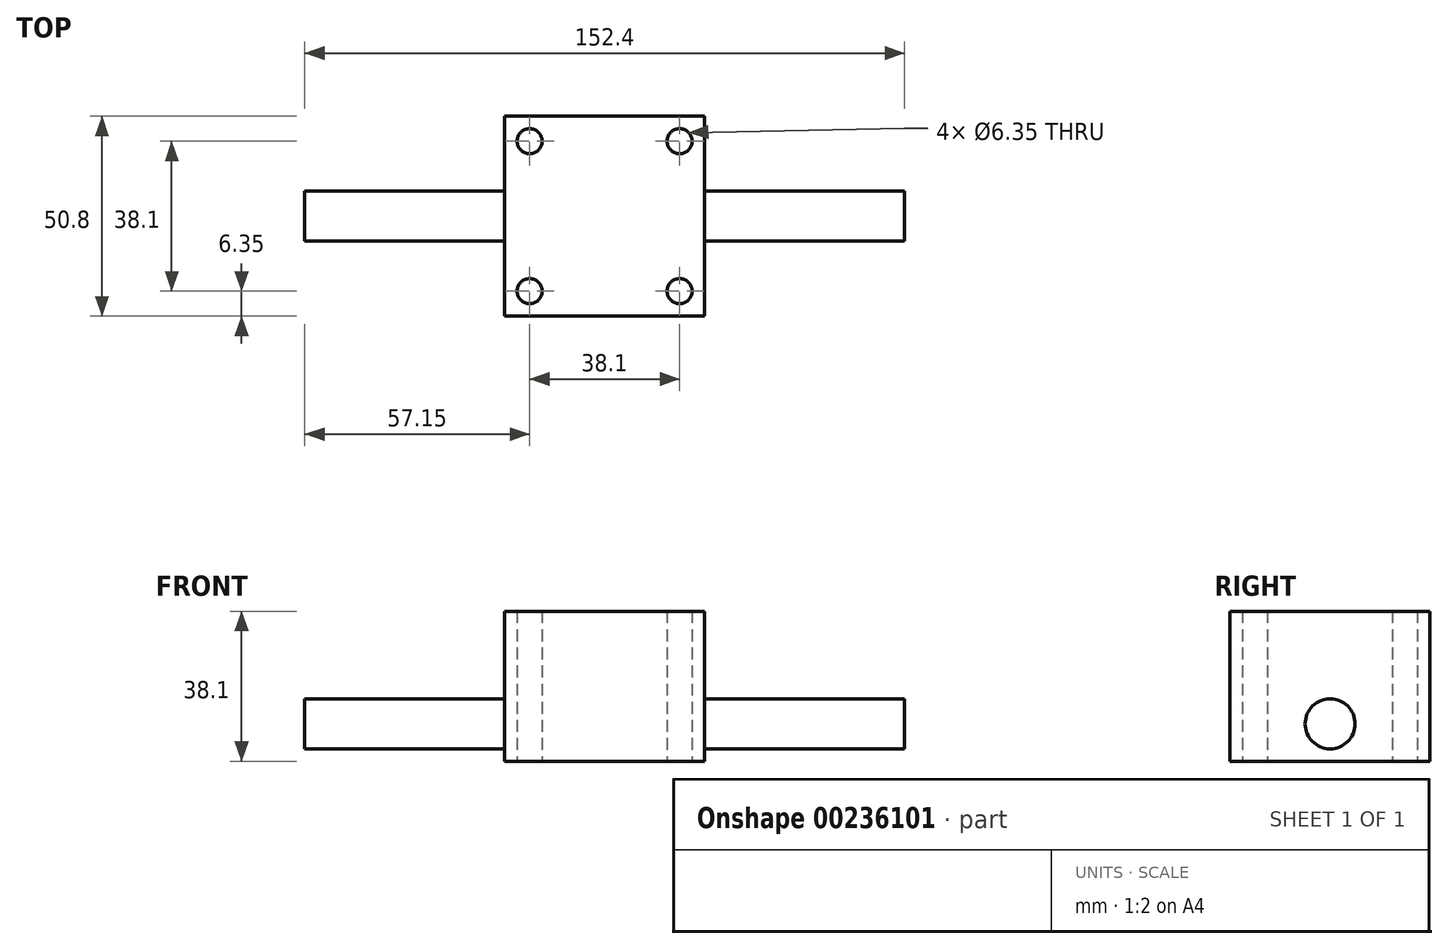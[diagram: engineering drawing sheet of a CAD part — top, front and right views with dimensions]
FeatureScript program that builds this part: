
annotation { "Feature Type Name" : "Feature", "Feature Type Description" : "" }
export const myFeature = defineFeature(function(context is Context, id is Id, definition is map)
    precondition{}
    {
        {
            var Q0;
            Q0=qCreatedBy(makeId("Top.planeOp"),FACE);
            var sketch = newSketch(context, id + "F0", { "sketchPlane" : qUnion([Q0])});
            skLineSegment(sketch, "E0.bottom", {"start": v(-25.4, 25.4) * mm, "end": v(25.4, 25.4) * mm});
            skLineSegment(sketch, "E0.top", {"start": v(-25.4, -25.4) * mm, "end": v(25.4, -25.4) * mm});
            skLineSegment(sketch, "E0.left", {"start": v(-25.4, 25.4) * mm, "end": v(-25.4, -25.4) * mm});
            skLineSegment(sketch, "E0.right", {"start": v(25.4, 25.4) * mm, "end": v(25.4, -25.4) * mm});
            skPoint(sketch, "E0.middle", {"position": v(0, 0) * mm});
            skCircle(sketch, "E1", {"center": v(-19.05, 19.05) * mm, "radius": 3.18 * mm});
            skCircle(sketch, "E2.MirrorC", {"center": v(19.05, 19.05) * mm, "radius": 3.18 * mm});
            skCircle(sketch, "E3.MirrorC", {"center": v(-19.05, -19.05) * mm, "radius": 3.18 * mm});
            skCircle(sketch, "E4.MirrorC", {"center": v(19.05, -19.05) * mm, "radius": 3.18 * mm});
            skSolve(sketch);
        }
        {
            var Q0;
            Q0 = qSketchRegion(id + "F0", true);
            extrude(context, id + "F1", {"entities" : qUnion([Q0]), "endBound" : BoundingType.SYMMETRIC, "depth" : 38.1 * mm});
        }
        {
            var Q0;
            Q0=qCreatedBy(makeId("Right.planeOp"),FACE);
            var sketch = newSketch(context, id + "F2", { "sketchPlane" : qUnion([Q0])});
            skCircle(sketch, "E5", {"center": v(0, -9.53) * mm, "radius": 6.35 * mm});
            skSolve(sketch);
        }
        {
            var Q0;
            Q0 = qSketchRegion(id + "F2", true);
            extrude(context, id + "F3", {"entities" : qUnion([Q0]), "operationType" : NewBodyOperationType.ADD, "endBound" : BoundingType.SYMMETRIC, "depth" : 152.4 * mm});
        }
    });
